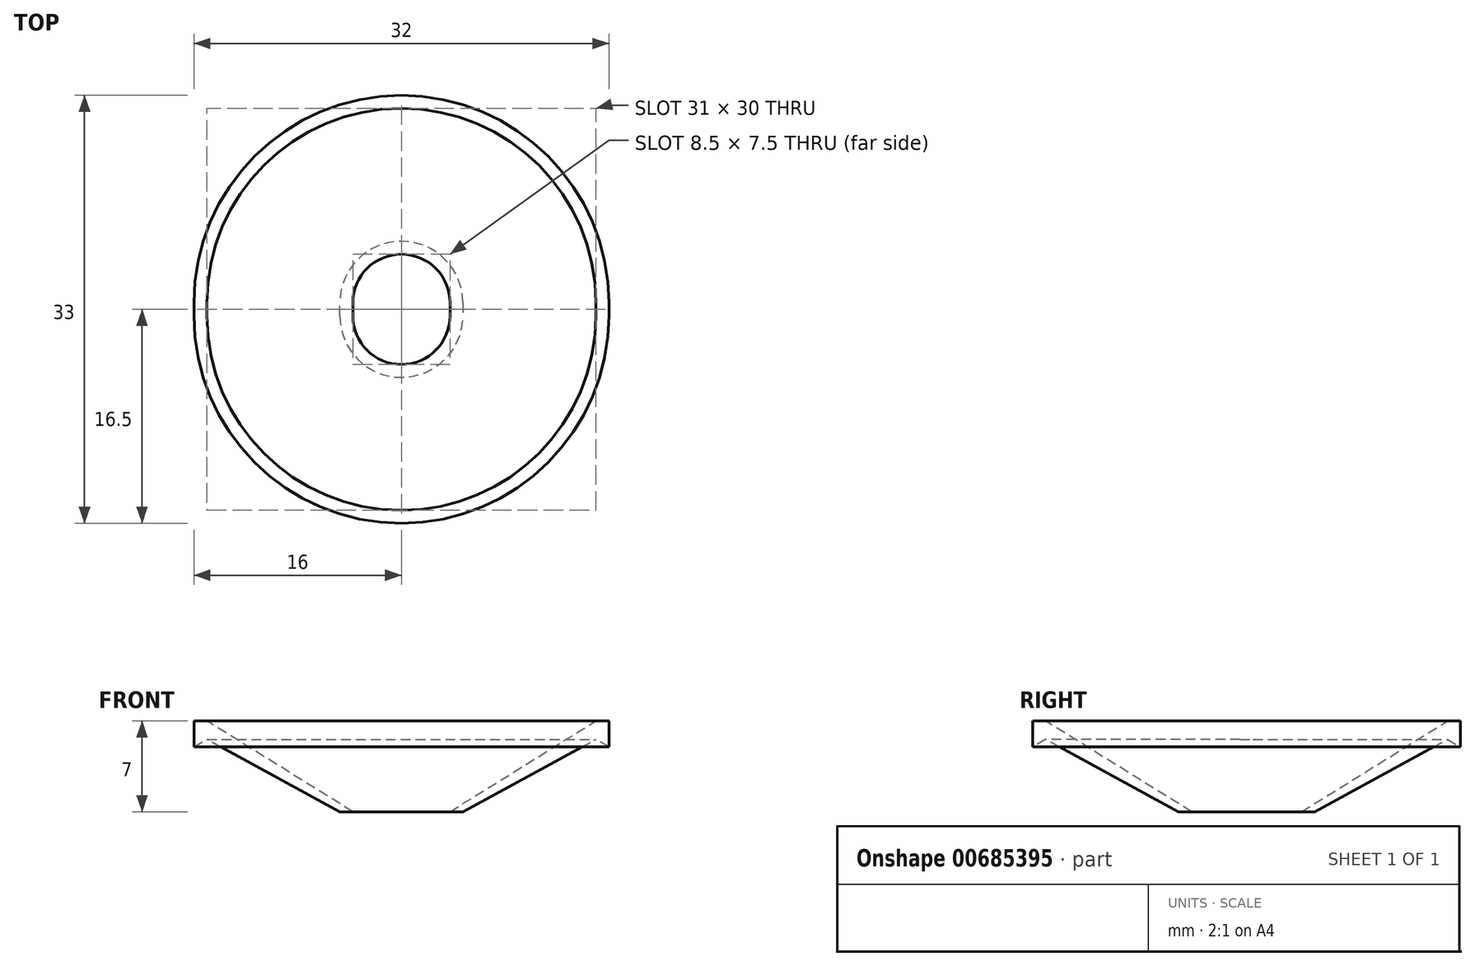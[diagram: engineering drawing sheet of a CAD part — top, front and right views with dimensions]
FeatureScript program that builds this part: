
annotation { "Feature Type Name" : "Feature", "Feature Type Description" : "" }
export const myFeature = defineFeature(function(context is Context, id is Id, definition is map)
    precondition{}
    {
        {
            var Q0;
            Q0=qCreatedBy(makeId("Top.planeOp"),FACE);
            var sketch = newSketch(context, id + "F0", { "sketchPlane" : qUnion([Q0])});
            skLineSegment(sketch, "E0.left", {"start": v(3.75, 0.5) * mm, "end": v(3.75, -0.5) * mm});
            skLineSegment(sketch, "E0.right", {"start": v(-3.75, 0.5) * mm, "end": v(-3.75, -0.5) * mm});
            skPoint(sketch, "E0.middle", {"position": v(0, 0) * mm});
            skArc(sketch, "E1", {"start": v(4.75, 0.5) * mm, "mid": v(0, 5.25) * mm, "end": v(-4.75, 0.5) * mm});
            skArc(sketch, "E2", {"start": v(-4.75, -0.5) * mm, "mid": v(0, -5.25) * mm, "end": v(4.75, -0.5) * mm});
            skLineSegment(sketch, "E3.left", {"start": v(4.75, 0.5) * mm, "end": v(4.75, -0.5) * mm});
            skLineSegment(sketch, "E3.right", {"start": v(-4.75, 0.5) * mm, "end": v(-4.75, -0.5) * mm});
            skArc(sketch, "E4.trimOffspring", {"start": v(-3.75, -0.5) * mm, "mid": v(0, -4.25) * mm, "end": v(3.75, -0.5) * mm});
            skArc(sketch, "E5.trimOffspring", {"start": v(3.75, 0.5) * mm, "mid": v(0, 4.25) * mm, "end": v(-3.75, 0.5) * mm});
            skSolve(sketch);
        }
        {
            var Q0;
            Q0=qCreatedBy(makeId("Front.planeOp"),FACE);
            var sketch = newSketch(context, id + "F1", { "sketchPlane" : qUnion([Q0])});
            skLineSegment(sketch, "E6", {"start": v(4.75, 0) * mm, "end": v(15, 5.58) * mm});
            skLineSegment(sketch, "E7", {"start": v(3.75, 0) * mm, "end": v(15, 7) * mm});
            skLineSegment(sketch, "E8.top", {"start": v(15, 7) * mm, "end": v(16, 7) * mm});
            skLineSegment(sketch, "E8.right", {"start": v(15, 7) * mm, "end": v(16, 7) * mm});
            skLineSegment(sketch, "E9", {"start": v(3.75, 0) * mm, "end": v(4.75, 0) * mm});
            skLineSegment(sketch, "E10", {"start": v(16, 7) * mm, "end": v(16, 5) * mm});
            skLineSegment(sketch, "E11", {"start": v(16, 5) * mm, "end": v(15, 5.58) * mm});
            skSolve(sketch);
        }
        {
            var Q0;
            Q0 = qSketchRegion(id + "F1", true);
            var Q1;
            Q1=sQuery(id+"F0.wireOp",EDGE,"E1");
            var Q2;
            Q2=sQuery(id+"F0.wireOp",EDGE,"E3.right");
            var Q3;
            Q3=sQuery(id+"F0.wireOp",EDGE,"E2");
            var Q4;
            Q4=sQuery(id+"F0.wireOp",EDGE,"E3.left");
            sweep(context, id + "F2", {"profiles" : qUnion([Q0]), "path" : qUnion([Q1, Q2, Q3, Q4])});
        }
    });
